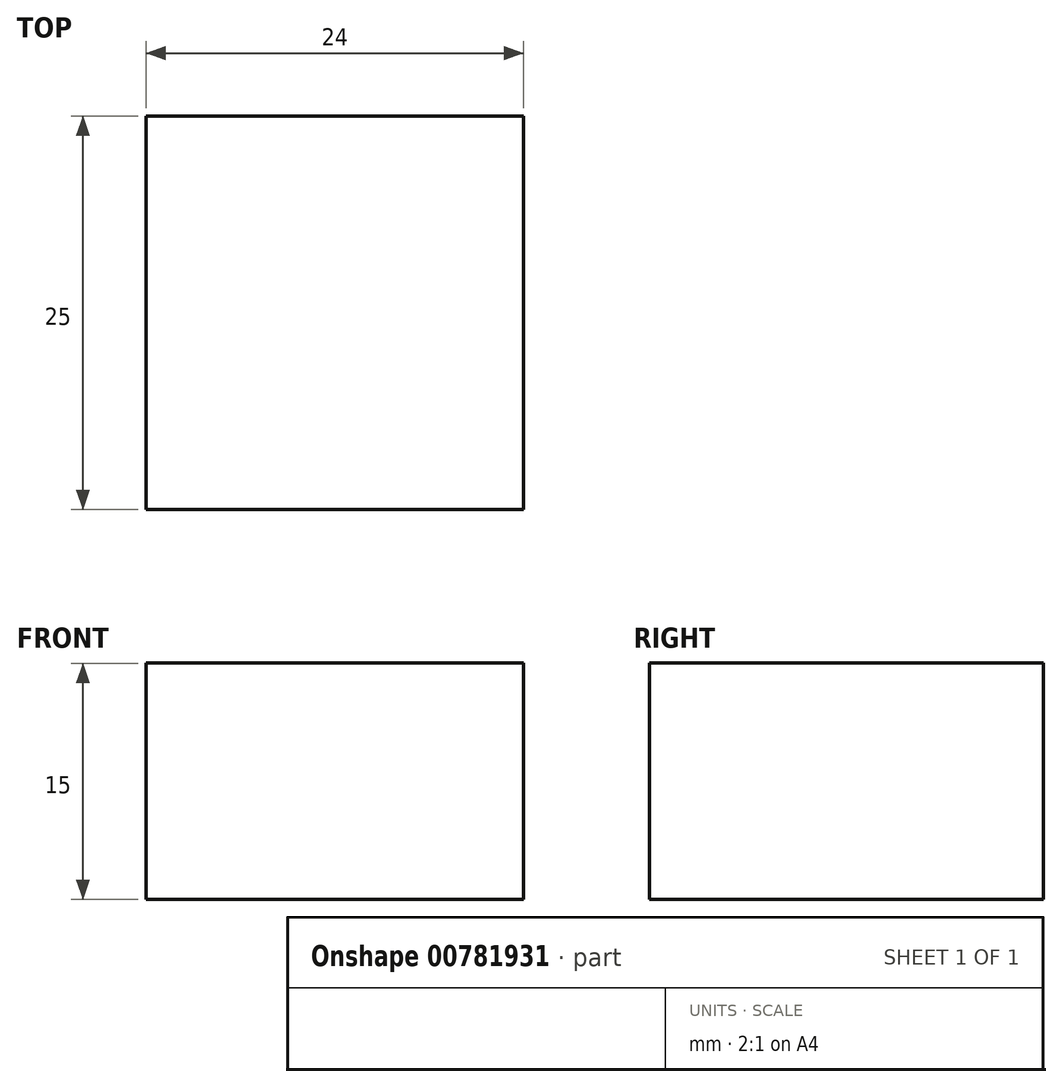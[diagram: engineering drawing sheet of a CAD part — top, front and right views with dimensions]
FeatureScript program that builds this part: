
annotation { "Feature Type Name" : "Feature", "Feature Type Description" : "" }
export const myFeature = defineFeature(function(context is Context, id is Id, definition is map)
    precondition{}
    {
        {
            var Q0;
            Q0=qCreatedBy(makeId("Front.planeOp"),FACE);
            var sketch = newSketch(context, id + "F0", { "sketchPlane" : qUnion([Q0])});
            skLineSegment(sketch, "E0.bottom", {"start": v(11.71, 2.54) * mm, "end": v(-13.29, 2.54) * mm});
            skLineSegment(sketch, "E0.top", {"start": v(11.71, -12.46) * mm, "end": v(-18.29, -12.46) * mm});
            skLineSegment(sketch, "E0.left", {"start": v(11.71, 2.54) * mm, "end": v(11.71, -12.46) * mm});
            skLineSegment(sketch, "E0.right", {"start": v(-12.29, 12.54) * mm, "end": v(-12.29, -12.46) * mm});
            skSolve(sketch);
        }
        {
            var Q0;
            Q0=qSketchRegion(id+"F0",true);
            extrude(context, id + "F1", {"entities" : qUnion([Q0]), "endBound" : BoundingType.SYMMETRIC, "depth" : 25 * mm, "offsetDistance" : 25 * mm});
        }
    });
